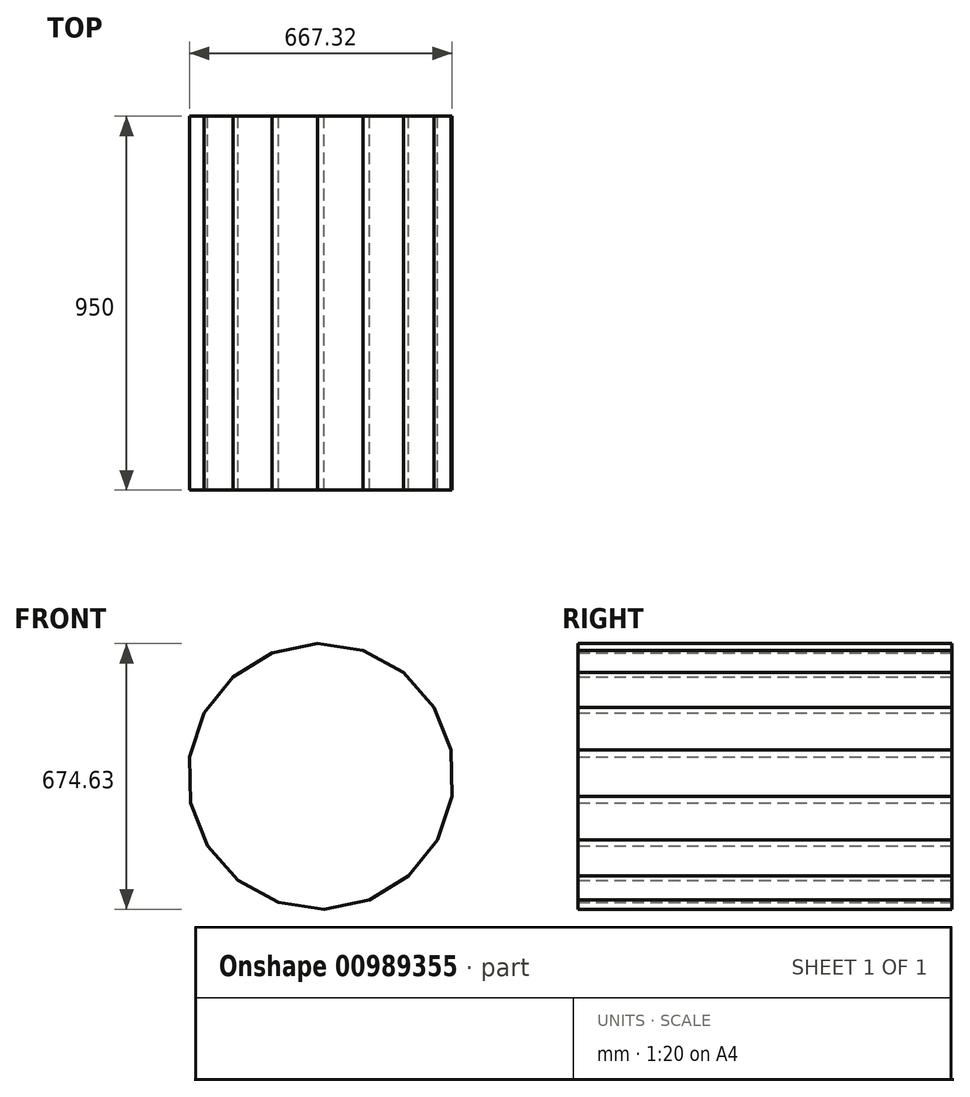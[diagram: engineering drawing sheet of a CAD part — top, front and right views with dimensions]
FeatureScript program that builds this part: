
annotation { "Feature Type Name" : "Feature", "Feature Type Description" : "" }
export const myFeature = defineFeature(function(context is Context, id is Id, definition is map)
    precondition{}
    {
        {
            var Q0;
            Q0=qCreatedBy(makeId("Front.planeOp"),FACE);
            var sketch = newSketch(context, id + "F0", { "sketchPlane" : qUnion([Q0])});
            skCircle(sketch, "E0.cCircle", {"center": v(-646.63, -143.34) * mm, "radius": 332.3 * mm, "construction": true});
            skLineSegment(sketch, "E0.0", {"start": v(-315.9, -76.45) * mm, "end": v(-312.97, -193.6) * mm});
            skLineSegment(sketch, "E0.1", {"start": v(-312.97, -193.6) * mm, "end": v(-350.28, -304.69) * mm});
            skLineSegment(sketch, "E0.2", {"start": v(-350.28, -304.69) * mm, "end": v(-423.33, -396.31) * mm});
            skLineSegment(sketch, "E0.3", {"start": v(-423.33, -396.31) * mm, "end": v(-523.32, -457.43) * mm});
            skLineSegment(sketch, "E0.4", {"start": v(-523.32, -457.43) * mm, "end": v(-638.18, -480.66) * mm});
            skLineSegment(sketch, "E0.5", {"start": v(-638.18, -480.66) * mm, "end": v(-754.06, -463.2) * mm});
            skLineSegment(sketch, "E0.6", {"start": v(-754.06, -463.2) * mm, "end": v(-856.98, -407.17) * mm});
            skLineSegment(sketch, "E0.7", {"start": v(-856.98, -407.17) * mm, "end": v(-934.53, -319.32) * mm});
            skLineSegment(sketch, "E0.8", {"start": v(-934.53, -319.32) * mm, "end": v(-977.35, -210.24) * mm});
            skLineSegment(sketch, "E0.9", {"start": v(-977.35, -210.24) * mm, "end": v(-980.29, -93.09) * mm});
            skLineSegment(sketch, "E0.10", {"start": v(-980.29, -93.09) * mm, "end": v(-942.98, 18) * mm});
            skLineSegment(sketch, "E0.11", {"start": v(-942.98, 18) * mm, "end": v(-869.92, 109.63) * mm});
            skLineSegment(sketch, "E0.12", {"start": v(-869.92, 109.63) * mm, "end": v(-769.93, 170.74) * mm});
            skLineSegment(sketch, "E0.13", {"start": v(-769.93, 170.74) * mm, "end": v(-655.07, 193.97) * mm});
            skLineSegment(sketch, "E0.14", {"start": v(-655.07, 193.97) * mm, "end": v(-539.2, 176.52) * mm});
            skLineSegment(sketch, "E0.15", {"start": v(-539.2, 176.52) * mm, "end": v(-436.27, 120.49) * mm});
            skLineSegment(sketch, "E0.16", {"start": v(-436.27, 120.49) * mm, "end": v(-358.72, 32.63) * mm});
            skLineSegment(sketch, "E0.17", {"start": v(-358.72, 32.63) * mm, "end": v(-315.9, -76.45) * mm});
            skPoint(sketch, "E0.0.midPoint", {"position": v(-314.43, -135.02) * mm});
            skSolve(sketch);
        }
        {
            var Q0;
            Q0=makeQuery(id+"F0.imprint","IMPRINT",FACE,{"disambiguationData":[TD([[makeQuery(id+"F0.imprint","IMPRINT",EDGE,{"derivedFrom":sQuery(id+"F0.wireOp",EDGE,"E0.0")}),-1.0]])]});
            extrude(context, id + "F1", {"entities" : qUnion([Q0]), "depth" : 950 * mm, "offsetDistance" : 25 * mm});
        }
    });
